# Revit family: Gira_057000
name_source: partatom
category: Allgemeines Modell
revit_build: Autodesk Revit 2017 (Build: 20160225_1515(x64)
units: mm (PartAtom-declared; Revit-internal decimal feet)

## family parameters
Basisbauteil = Fläche
Beim Laden mit Abzugskörper schneiden = Nein
Bemaßung runder Anschluss = Durchmesser verwenden
Gemeinsam genutzt = Nein
Kann Basisbauteil für Bewehrung sein = Nein
Raumberechnungspunkt = Nein
Teiletyp = Normal

## types (1)
- Busankoppler KNX Einsatz
    Andere Bussysteme = ohne
    BIM = https://media.stage.bim.site
    BIMSITE_PRODUCT_ID = bc3e54458c7a90461a68c8f00fad60ed08584449
    Befestigungsart = Krallen-/Schraubbefestigung
    Beschreibung = Einsatz KNX Busankoppler   Merkmale:  Der Busankoppler ist die Schnittstelle zwischen dem Bus und dem KNX Anwendungsmodul wie z. B. Info-Display, Datenschnittstelle RS232, Automatikschalter.  Die Busankopplung kann Telegramme empfangen, aussenden und auswerten.  Die Busankopplung enthält die Adressen, das Systemprogramm und auch anwenderspezifische Programme.  Freigabe der Programmierung der physikalischen Adresse durch Betätigen der Programmiertaste.  Zustandsanzeige durch rote Programmier-LED.  Hinweise :  Nur für Gerätedose mit Schraubbefestigung geeignet.
    Bussystem Funkbus = Nein
    Bussystem KNX = Ja
    Bussystem KNX-Funk = Nein
    Bussystem LON = Nein
    Bussystem Powernet = Nein
    Datenblatt = https://media.stage.bim.site
    Datenblatt 1 = https://media.stage.bim.site
    GTIN = 4010337570004
    HAN = 057000
    HeinzeBIM = https://www.heinze.de
    Hersteller = Gira
    Kosten = 0 $
    Montageart = Unterputz
    Produktseite = https://media.stage.bim.site
    Typname = Busankoppler KNX Einsatz
    URL = https://www.gira.de
    Vorgabe-Ansicht = 1219 mm

## geometry (parser evidence)
native form markers: Sweep x2
no freeform markers — native parametric forms only
